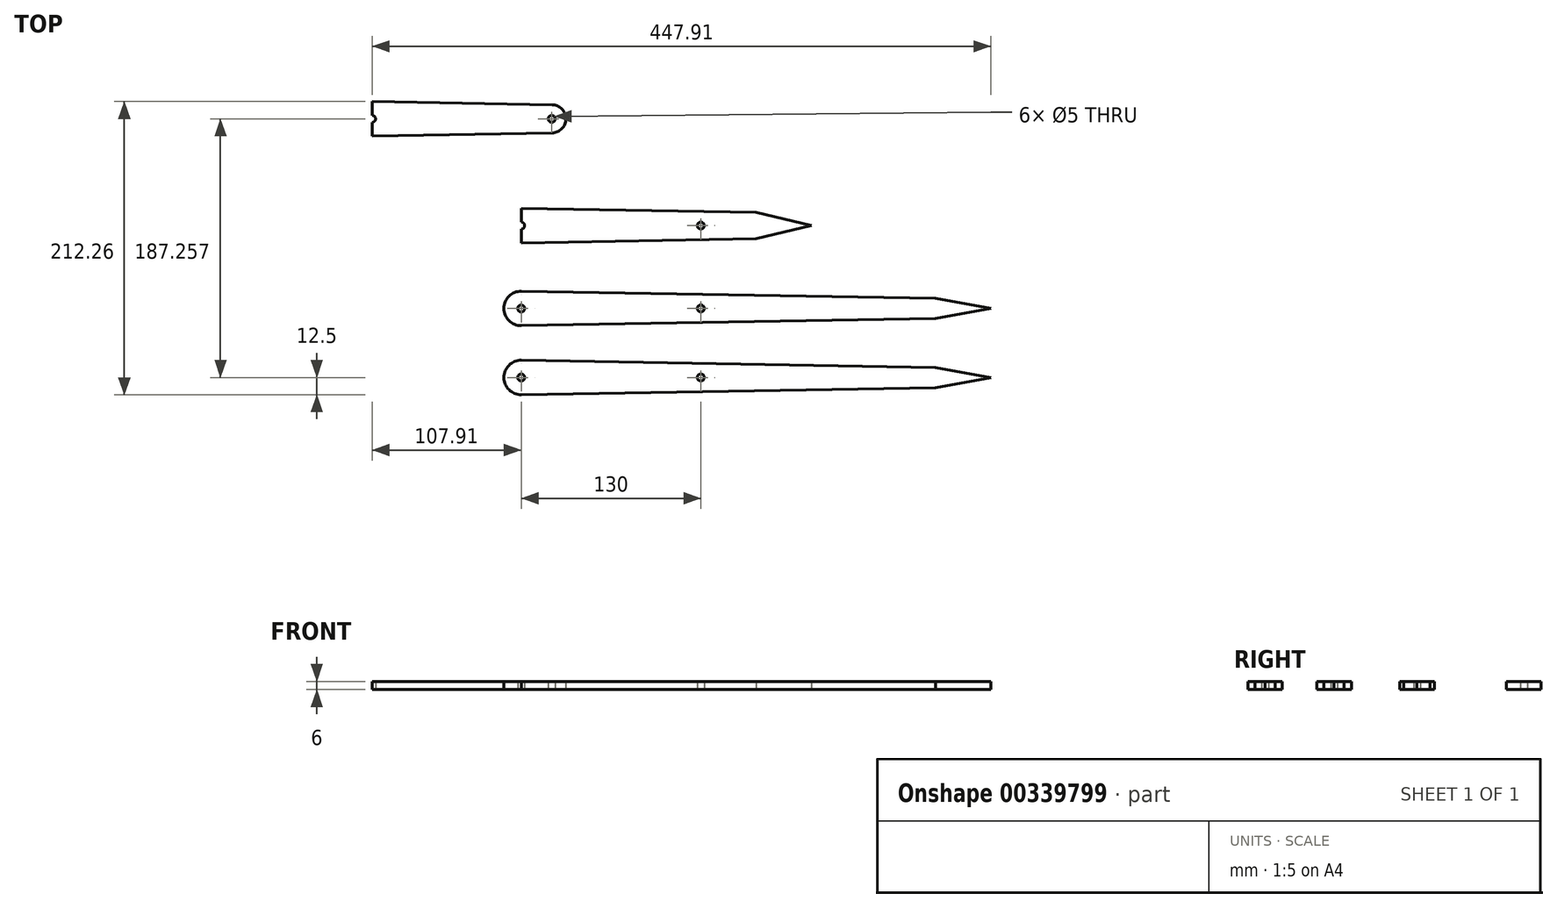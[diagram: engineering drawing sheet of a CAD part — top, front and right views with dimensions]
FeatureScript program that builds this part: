
annotation { "Feature Type Name" : "Feature", "Feature Type Description" : "" }
export const myFeature = defineFeature(function(context is Context, id is Id, definition is map)
    precondition{}
    {
        {
            var Q0;
            Q0=qCreatedBy(makeId("Top.planeOp"),FACE);
            var sketch = newSketch(context, id + "F0", { "sketchPlane" : qUnion([Q0])});
            skArc(sketch, "E0", {"start": v(0, 12.5) * mm, "mid": v(-12.5, 0) * mm, "end": v(0, -12.5) * mm});
            skCircle(sketch, "E1", {"center": v(0, 0) * mm, "radius": 2.5 * mm});
            skCircle(sketch, "E2", {"center": v(130, 0) * mm, "radius": 2.5 * mm});
            skPoint(sketch, "E3", {"position": v(340, 0) * mm});
            skLineSegment(sketch, "E4", {"start": v(0, 12.5) * mm, "end": v(300, 7.3) * mm});
            skLineSegment(sketch, "E5", {"start": v(0, -12.5) * mm, "end": v(300, -7.3) * mm});
            skLineSegment(sketch, "E6", {"start": v(340, 0) * mm, "end": v(300, -7.3) * mm});
            skLineSegment(sketch, "E7", {"start": v(340, 0) * mm, "end": v(300, 7.3) * mm});
            skSolve(sketch);
        }
        {
            var Q0;
            Q0=makeQuery(id+"F0.imprint","IMPRINT",FACE,{"disambiguationData":[TD([[makeQuery(id+"F0.imprint","IMPRINT",EDGE,{"derivedFrom":sQuery(id+"F0.wireOp",EDGE,"E0")}),1.0]])]});
            extrude(context, id + "F1", {"entities" : qUnion([Q0]), "depth" : 6 * mm});
        }
        {
            var Q0;
            Q0=makeQuery(id+"F1.opExtrude","SWEPT_BODY",BODY,{"disambiguationData":[OSD([sQuery(id+"F0.wireOp",EDGE,"E0"),sQuery(id+"F0.wireOp",EDGE,"E1"),sQuery(id+"F0.wireOp",EDGE,"E2"),sQuery(id+"F0.wireOp",EDGE,"E4"),sQuery(id+"F0.wireOp",EDGE,"E5"),sQuery(id+"F0.wireOp",EDGE,"E6"),sQuery(id+"F0.wireOp",EDGE,"E7")])]});
            transform(context, id + "F2", {"entities" : qUnion([Q0]), "transformType" : TransformType.TRANSLATION_3D, "dx" : 0 * mm, "dy" : 50 * mm, "dz" : 0 * mm, "makeCopy" : true});
        }
        {
            var Q0;
            Q0=makeQuery(id+"F2.opPattern","COPY",BODY,{"derivedFrom":makeQuery(id+"F1.opExtrude","SWEPT_BODY",BODY,{"disambiguationData":[OSD([sQuery(id+"F0.wireOp",EDGE,"E0"),sQuery(id+"F0.wireOp",EDGE,"E1"),sQuery(id+"F0.wireOp",EDGE,"E2"),sQuery(id+"F0.wireOp",EDGE,"E4"),sQuery(id+"F0.wireOp",EDGE,"E5"),sQuery(id+"F0.wireOp",EDGE,"E6"),sQuery(id+"F0.wireOp",EDGE,"E7")])]}),"instanceName":"1"});
            transform(context, id + "F3", {"entities" : qUnion([Q0]), "transformType" : TransformType.TRANSLATION_3D, "dx" : 0 * mm, "dy" : 50 * mm, "dz" : 0 * mm, "makeCopy" : true});
        }
        {
            var Q0;
            Q0=makeQuery(id+"F3.opPattern","COPY",BODY,{"derivedFrom":makeQuery(id+"F2.opPattern","COPY",BODY,{"derivedFrom":makeQuery(id+"F1.opExtrude","SWEPT_BODY",BODY,{"disambiguationData":[OSD([sQuery(id+"F0.wireOp",EDGE,"E0"),sQuery(id+"F0.wireOp",EDGE,"E1"),sQuery(id+"F0.wireOp",EDGE,"E2"),sQuery(id+"F0.wireOp",EDGE,"E4"),sQuery(id+"F0.wireOp",EDGE,"E5"),sQuery(id+"F0.wireOp",EDGE,"E6"),sQuery(id+"F0.wireOp",EDGE,"E7")])]}),"instanceName":"1"}),"instanceName":"1"});
            deleteBodies(context, id + "F4", {"entities" : qUnion([Q0])});
        }
        {
            var Q0;
            Q0=qCreatedBy(makeId("Top.planeOp"),FACE);
            var sketch = newSketch(context, id + "F5", { "sketchPlane" : qUnion([Q0])});
            skCircle(sketch, "E8", {"center": v(0, 109.99) * mm, "radius": 12.5 * mm});
            skLineSegment(sketch, "E9.left", {"start": v(0, 122.49) * mm, "end": v(0, 97.49) * mm});
            skLineSegment(sketch, "E9.right", {"start": v(210, 122.49) * mm, "end": v(210, 97.49) * mm});
            skPoint(sketch, "E10", {"position": v(210, 109.99) * mm});
            skCircle(sketch, "E11", {"center": v(0, 109.99) * mm, "radius": 2.5 * mm});
            skCircle(sketch, "E12", {"center": v(130, 109.99) * mm, "radius": 2.5 * mm});
            skLineSegment(sketch, "E13", {"start": v(0, 122.49) * mm, "end": v(210, 118.82) * mm});
            skLineSegment(sketch, "E14", {"start": v(0, 97.49) * mm, "end": v(210, 101.15) * mm});
            skLineSegment(sketch, "E15", {"start": v(0, 109.99) * mm, "end": v(130, 109.99) * mm, "construction": true});
            skLineSegment(sketch, "E16", {"start": v(210, 109.99) * mm, "end": v(170, 119.52) * mm});
            skLineSegment(sketch, "E17", {"start": v(210, 109.99) * mm, "end": v(170, 100.45) * mm});
            skSolve(sketch);
        }
        {
            var Q0;
            Q0=makeQuery(id+"F5.imprint","IMPRINT",FACE,{"disambiguationData":[TD([[makeQuery(id+"F5.imprint","IMPRINT",EDGE,{"derivedFrom":sQuery(id+"F5.wireOp",EDGE,"E12")}),-1.0]])]});
            var Q1;
            {var subQ5=sQuery(id+"F5.wireOp",EDGE,"E8");var subQ7=sQuery(id+"F5.wireOp",EDGE,"E13");var subQ9=makeQuery(id+"F5.imprint","INTERSECT",VERTEX,{"derivedFrom":[subQ5,subQ7]});Q1=makeQuery(id+"F5.imprint","IMPRINT",FACE,{"disambiguationData":[TD([[makeQuery(id+"F5.imprint","IMPRINT",EDGE,{"disambiguationData":[TD([[subQ9,1.0]])],"derivedFrom":subQ5}),1.0]])]});}
            var Q2;
            {var subQ0=sQuery(id+"F5.wireOp",EDGE,"E9.left");var subQ4=sQuery(id+"F5.wireOp",EDGE,"E11");var subQ5=makeQuery(id+"F5.imprint","INTERSECT",VERTEX,{"disambiguationData":[OD(0.0)],"derivedFrom":[subQ0,subQ4]});Q2=makeQuery(id+"F5.imprint","IMPRINT",FACE,{"disambiguationData":[TD([[makeQuery(id+"F5.imprint","IMPRINT",EDGE,{"disambiguationData":[TD([[subQ5,-1.0]])],"derivedFrom":subQ4}),-1.0]])]});}
            extrude(context, id + "F6", {"entities" : qUnion([Q0, Q1, Q2]), "depth" : 6 * mm});
        }
        {
            var Q0;
            Q0=qCreatedBy(makeId("Top.planeOp"),FACE);
            var sketch = newSketch(context, id + "F7", { "sketchPlane" : qUnion([Q0])});
            skArc(sketch, "E18", {"start": v(-107.47, 199.75) * mm, "mid": v(-120.4, 187.26) * mm, "end": v(-107.47, 174.76) * mm});
            skLineSegment(sketch, "E19.left", {"start": v(-107.9, 199.76) * mm, "end": v(-107.9, 174.76) * mm});
            skCircle(sketch, "E20", {"center": v(-107.9, 187.26) * mm, "radius": 2.5 * mm});
            skCircle(sketch, "E21", {"center": v(22.1, 187.26) * mm, "radius": 2.5 * mm});
            skLineSegment(sketch, "E22", {"start": v(-107.9, 199.76) * mm, "end": v(22.27, 197.48) * mm});
            skLineSegment(sketch, "E23", {"start": v(-107.9, 174.76) * mm, "end": v(22.27, 177.03) * mm});
            skLineSegment(sketch, "E24", {"start": v(-107.9, 187.26) * mm, "end": v(22.1, 187.26) * mm, "construction": true});
            skArc(sketch, "E25", {"start": v(22.27, 177.03) * mm, "mid": v(32.32, 187.26) * mm, "end": v(22.27, 197.48) * mm});
            skSolve(sketch);
        }
        {
            var Q0;
            Q0=makeQuery(id+"F7.imprint","IMPRINT",FACE,{"disambiguationData":[TD([[makeQuery(id+"F7.imprint","IMPRINT",EDGE,{"derivedFrom":sQuery(id+"F7.wireOp",EDGE,"E21")}),-1.0]])]});
            var Q1;
            {var subQ0=sQuery(id+"F7.wireOp",EDGE,"E19.left");var subQ4=sQuery(id+"F7.wireOp",EDGE,"E20");var subQ5=makeQuery(id+"F7.imprint","INTERSECT",VERTEX,{"disambiguationData":[OD(0.0)],"derivedFrom":[subQ0,subQ4]});Q1=makeQuery(id+"F7.imprint","IMPRINT",FACE,{"disambiguationData":[TD([[makeQuery(id+"F7.imprint","IMPRINT",EDGE,{"disambiguationData":[TD([[subQ5,-1.0]])],"derivedFrom":subQ4}),-1.0]])]});}
            extrude(context, id + "F8", {"entities" : qUnion([Q0, Q1]), "depth" : 6 * mm});
        }
    });
